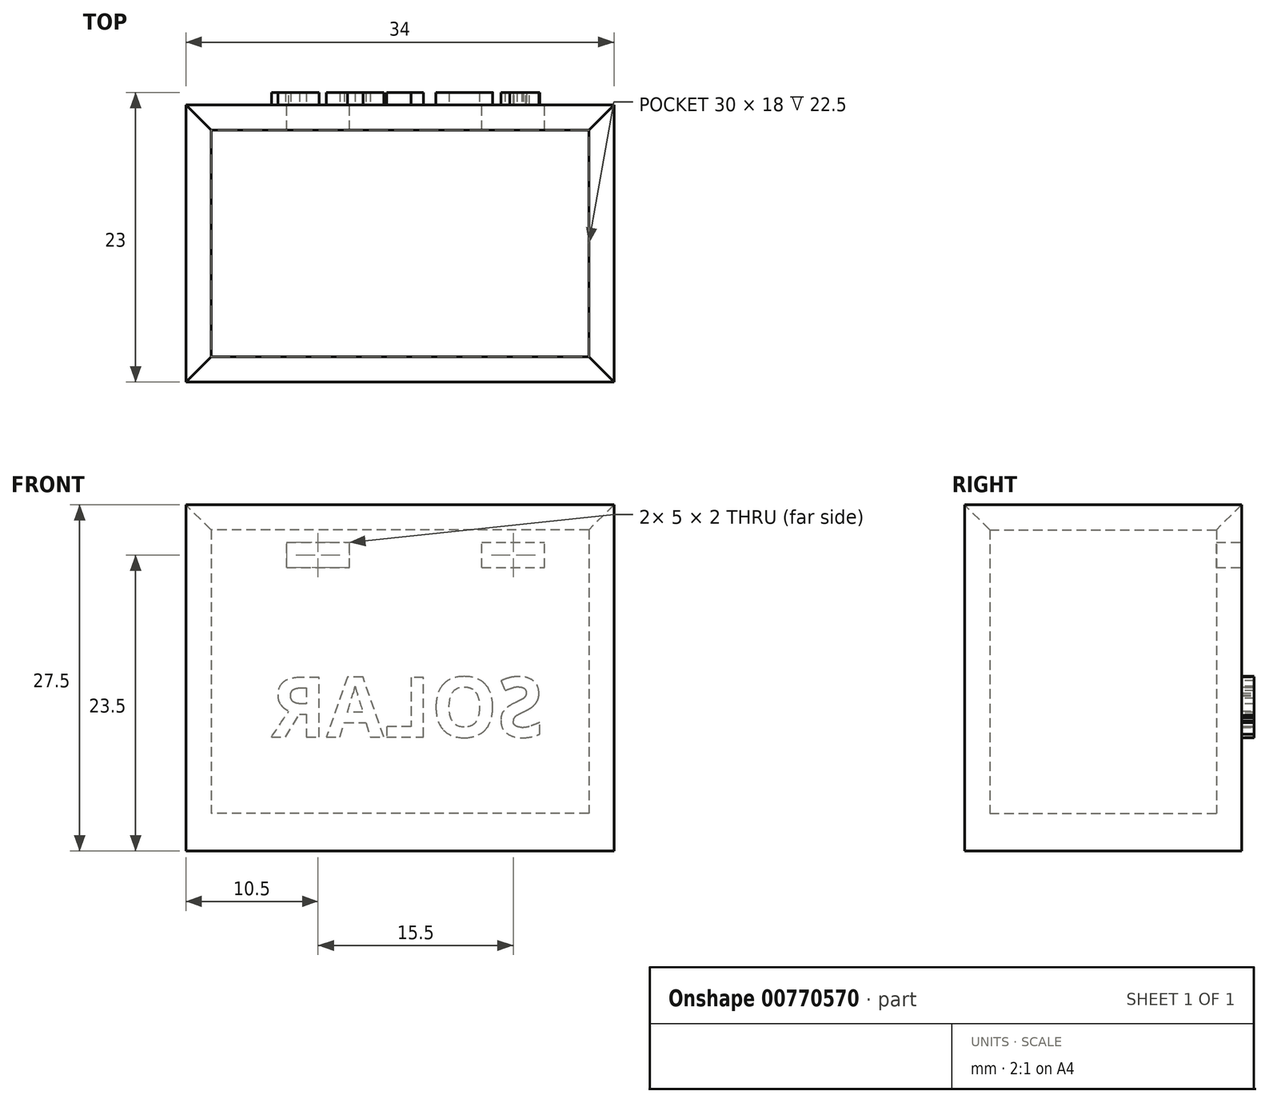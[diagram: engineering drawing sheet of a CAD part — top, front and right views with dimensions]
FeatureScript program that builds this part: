
annotation { "Feature Type Name" : "Feature", "Feature Type Description" : "" }
export const myFeature = defineFeature(function(context is Context, id is Id, definition is map)
    precondition{}
    {
        {
            var Q0;
            Q0=qCreatedBy(makeId("Top.planeOp"),FACE);
            var sketch = newSketch(context, id + "F0", { "sketchPlane" : qUnion([Q0])});
            skLineSegment(sketch, "E0.bottom", {"start": v(17, -11) * mm, "end": v(-17, -11) * mm});
            skLineSegment(sketch, "E0.top", {"start": v(17, 11) * mm, "end": v(-17, 11) * mm});
            skLineSegment(sketch, "E0.left", {"start": v(17, -11) * mm, "end": v(17, 11) * mm});
            skLineSegment(sketch, "E0.right", {"start": v(-17, -11) * mm, "end": v(-17, 11) * mm});
            skPoint(sketch, "E0.middle", {"position": v(0, 0) * mm});
            skSolve(sketch);
        }
        {
            var Q0;
            Q0=makeQuery(id+"F0.imprint","IMPRINT",FACE,{"disambiguationData":[TD([[makeQuery(id+"F0.imprint","IMPRINT",EDGE,{"derivedFrom":sQuery(id+"F0.wireOp",EDGE,"E0.bottom")}),-1.0]])]});
            extrude(context, id + "F1", {"entities" : qUnion([Q0]), "depth" : 3 * mm, "offsetDistance" : 25 * mm});
        }
        {
            var Q0;
            Q0=makeQuery(id+"F1.opExtrude","CAP_FACE",FACE,{"disambiguationData":[OSD([sQuery(id+"F0.wireOp",EDGE,"E0.bottom"),sQuery(id+"F0.wireOp",EDGE,"E0.top"),sQuery(id+"F0.wireOp",EDGE,"E0.left"),sQuery(id+"F0.wireOp",EDGE,"E0.right")])],"isStart":false});
            var sketch = newSketch(context, id + "F2", { "sketchPlane" : qUnion([Q0])});
            skLineSegment(sketch, "E1.bottom", {"start": v(15, -9) * mm, "end": v(-15, -9) * mm});
            skLineSegment(sketch, "E1.top", {"start": v(15, 9) * mm, "end": v(-15, 9) * mm});
            skLineSegment(sketch, "E1.left", {"start": v(15, -9) * mm, "end": v(15, 9) * mm});
            skLineSegment(sketch, "E1.right", {"start": v(-15, -9) * mm, "end": v(-15, 9) * mm});
            skPoint(sketch, "E1.middle", {"position": v(0, 0) * mm});
            skSolve(sketch);
        }
        {
            var Q0;
            Q0=makeQuery(id+"F2.imprint","IMPRINT",FACE,{"disambiguationData":[TD([[makeQuery(id+"F2.imprint","IMPRINT",EDGE,{"derivedFrom":sQuery(id+"F2.wireOp",EDGE,"E1.bottom")}),1.0]])]});
            extrude(context, id + "F3", {"entities" : qUnion([Q0]), "operationType" : NewBodyOperationType.ADD, "depth" : 24.5 * mm, "offsetDistance" : 25 * mm});
        }
        {
            var Q0;
            Q0=makeQuery(id+"F3.opExtrude","CAP_EDGE",EDGE,{"disambiguationData":[OSD([sQuery(id+"F2.wireOp",EDGE,"E1.right")])],"isStart":false});
            var Q1;
            Q1=makeQuery(id+"F3.opExtrude","CAP_EDGE",EDGE,{"disambiguationData":[OSD([sQuery(id+"F2.wireOp",EDGE,"E1.left")])],"isStart":false});
            var Q2;
            Q2=makeQuery(id+"F3.opExtrude","CAP_EDGE",EDGE,{"disambiguationData":[OSD([sQuery(id+"F2.wireOp",EDGE,"E1.bottom")])],"isStart":false});
            var Q3;
            Q3=makeQuery(id+"F3.opExtrude","CAP_EDGE",EDGE,{"disambiguationData":[OSD([sQuery(id+"F2.wireOp",EDGE,"E1.top")])],"isStart":false});
            chamfer(context, id + "F4", {"entities" : qUnion([Q0, Q1, Q2, Q3]), "width" : 2 * mm, "tangentPropagation" : true});
        }
        {
            var Q0;
            {var subQ0=sQuery(id+"F0.wireOp",EDGE,"E0.top");Q0=makeQuery(id+"F3.boolean.opBoolean","MERGE",FACE,{"derivedFrom":[makeQuery(id+"F1.opExtrude","SWEPT_FACE",FACE,{"disambiguationData":[OSD([subQ0])]}),makeQuery(id+"F3.opExtrude","SWEPT_FACE",FACE,{"disambiguationData":[OSD([subQ0])]})]});}
            var sketch = newSketch(context, id + "F5", { "sketchPlane" : qUnion([Q0])});
            skLineSegment(sketch, "E2.bottom", {"start": v(-6.5, 22.5) * mm, "end": v(-11.5, 22.5) * mm});
            skLineSegment(sketch, "E2.top", {"start": v(-6.5, 24.5) * mm, "end": v(-11.5, 24.5) * mm});
            skLineSegment(sketch, "E2.left", {"start": v(-6.5, 22.5) * mm, "end": v(-6.5, 24.5) * mm});
            skLineSegment(sketch, "E2.right", {"start": v(-11.5, 22.5) * mm, "end": v(-11.5, 24.5) * mm});
            skPoint(sketch, "E2.middle", {"position": v(-9, 23.5) * mm});
            skLineSegment(sketch, "E3.bottom", {"start": v(9, 22.5) * mm, "end": v(4, 22.5) * mm});
            skLineSegment(sketch, "E3.top", {"start": v(9, 24.5) * mm, "end": v(4, 24.5) * mm});
            skLineSegment(sketch, "E3.left", {"start": v(9, 22.5) * mm, "end": v(9, 24.5) * mm});
            skLineSegment(sketch, "E3.right", {"start": v(4, 22.5) * mm, "end": v(4, 24.5) * mm});
            skPoint(sketch, "E3.middle", {"position": v(6.5, 23.5) * mm});
            skSolve(sketch);
        }
        {
            var Q0;
            Q0=makeQuery(id+"F5.imprint","IMPRINT",FACE,{"disambiguationData":[TD([[makeQuery(id+"F5.imprint","IMPRINT",EDGE,{"derivedFrom":sQuery(id+"F5.wireOp",EDGE,"E2.bottom")}),-1.0]])]});
            var Q1;
            Q1=makeQuery(id+"F5.imprint","IMPRINT",FACE,{"disambiguationData":[TD([[makeQuery(id+"F5.imprint","IMPRINT",EDGE,{"derivedFrom":sQuery(id+"F5.wireOp",EDGE,"E3.bottom")}),-1.0]])]});
            extrude(context, id + "F6", {"entities" : qUnion([Q0, Q1]), "operationType" : NewBodyOperationType.REMOVE, "oppositeDirection" : true, "depth" : 2 * mm, "offsetDistance" : 25 * mm});
        }
        {
            var Q0;
            {var subQ0=sQuery(id+"F0.wireOp",EDGE,"E0.top");Q0=makeQuery(id+"F3.boolean.opBoolean","MERGE",FACE,{"derivedFrom":[makeQuery(id+"F1.opExtrude","SWEPT_FACE",FACE,{"disambiguationData":[OSD([subQ0])]}),makeQuery(id+"F3.opExtrude","SWEPT_FACE",FACE,{"disambiguationData":[OSD([subQ0])]})]});}
            var sketch = newSketch(context, id + "F7", { "sketchPlane" : qUnion([Q0])});
            skText(sketch, "E4", { "text": "SOLAR", "fontName": "OpenSans-Bold.ttf"});
            const initialGuessF7  = {"E4": [-0.0114, 0.00906, 1, 0, 0.00477]};
            skSetInitialGuess(sketch, initialGuessF7);
            skSolve(sketch);
        }
        {
            var Q0;
            Q0 = qSketchRegion(id + "F7", true);
            extrude(context, id + "F8", {"entities" : qUnion([Q0]), "operationType" : NewBodyOperationType.ADD, "depth" : 1 * mm, "offsetDistance" : 25 * mm});
        }
    });
